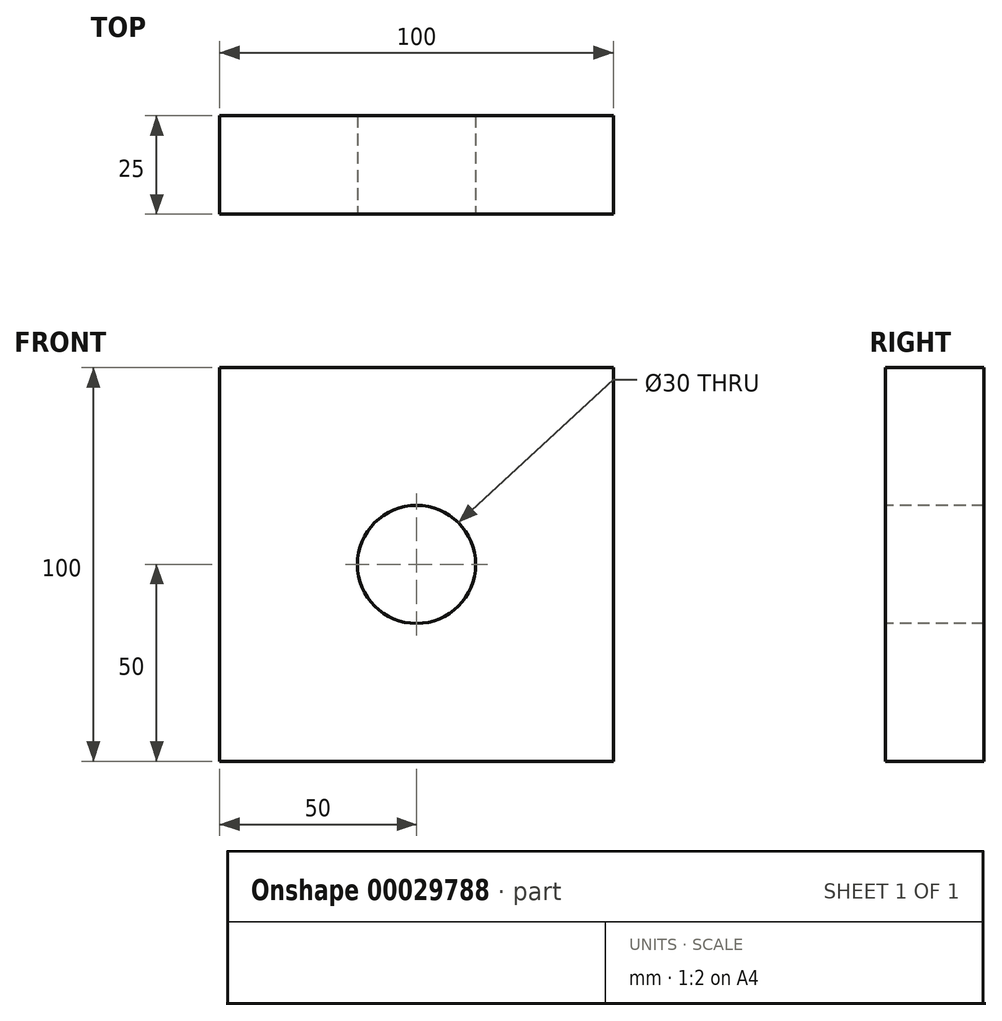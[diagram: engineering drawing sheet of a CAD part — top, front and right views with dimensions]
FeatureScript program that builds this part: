
annotation { "Feature Type Name" : "Feature", "Feature Type Description" : "" }
export const myFeature = defineFeature(function(context is Context, id is Id, definition is map)
    precondition{}
    {
        {
            var Q0;
            Q0=qCreatedBy(makeId("Front.planeOp"),FACE);
            var sketch = newSketch(context, id + "F0", { "sketchPlane" : qUnion([Q0])});
            skLineSegment(sketch, "E0.bottom", {"start": v(0, 0) * mm, "end": v(100, 0) * mm});
            skLineSegment(sketch, "E0.top", {"start": v(0, 100) * mm, "end": v(100, 100) * mm});
            skLineSegment(sketch, "E0.left", {"start": v(0, 0) * mm, "end": v(0, 100) * mm});
            skLineSegment(sketch, "E0.right", {"start": v(100, 0) * mm, "end": v(100, 100) * mm});
            skSolve(sketch);
        }
        {
            var Q0;
            Q0=qSketchRegion(id+"F0",true);
            extrude(context, id + "F1", {"entities" : qUnion([Q0]), "depth" : 25 * mm});
        }
        {
            var Q0;
            Q0=makeQuery(id+"F1.opExtrude","CAP_FACE",FACE,{"disambiguationData":[OSD([sQuery(id+"F0.wireOp",EDGE,"E0.bottom"),sQuery(id+"F0.wireOp",EDGE,"E0.top"),sQuery(id+"F0.wireOp",EDGE,"E0.left"),sQuery(id+"F0.wireOp",EDGE,"E0.right")])],"isStart":false});
            var sketch = newSketch(context, id + "F2", { "sketchPlane" : qUnion([Q0])});
            skCircle(sketch, "E1", {"center": v(50, 50) * mm, "radius": 15 * mm});
            skSolve(sketch);
        }
        {
            var Q0;
            Q0 = qSketchRegion(id + "F2", true);
            extrude(context, id + "F3", {"entities" : qUnion([Q0]), "operationType" : NewBodyOperationType.REMOVE, "oppositeDirection" : true, "depth" : 25 * mm});
        }
    });
